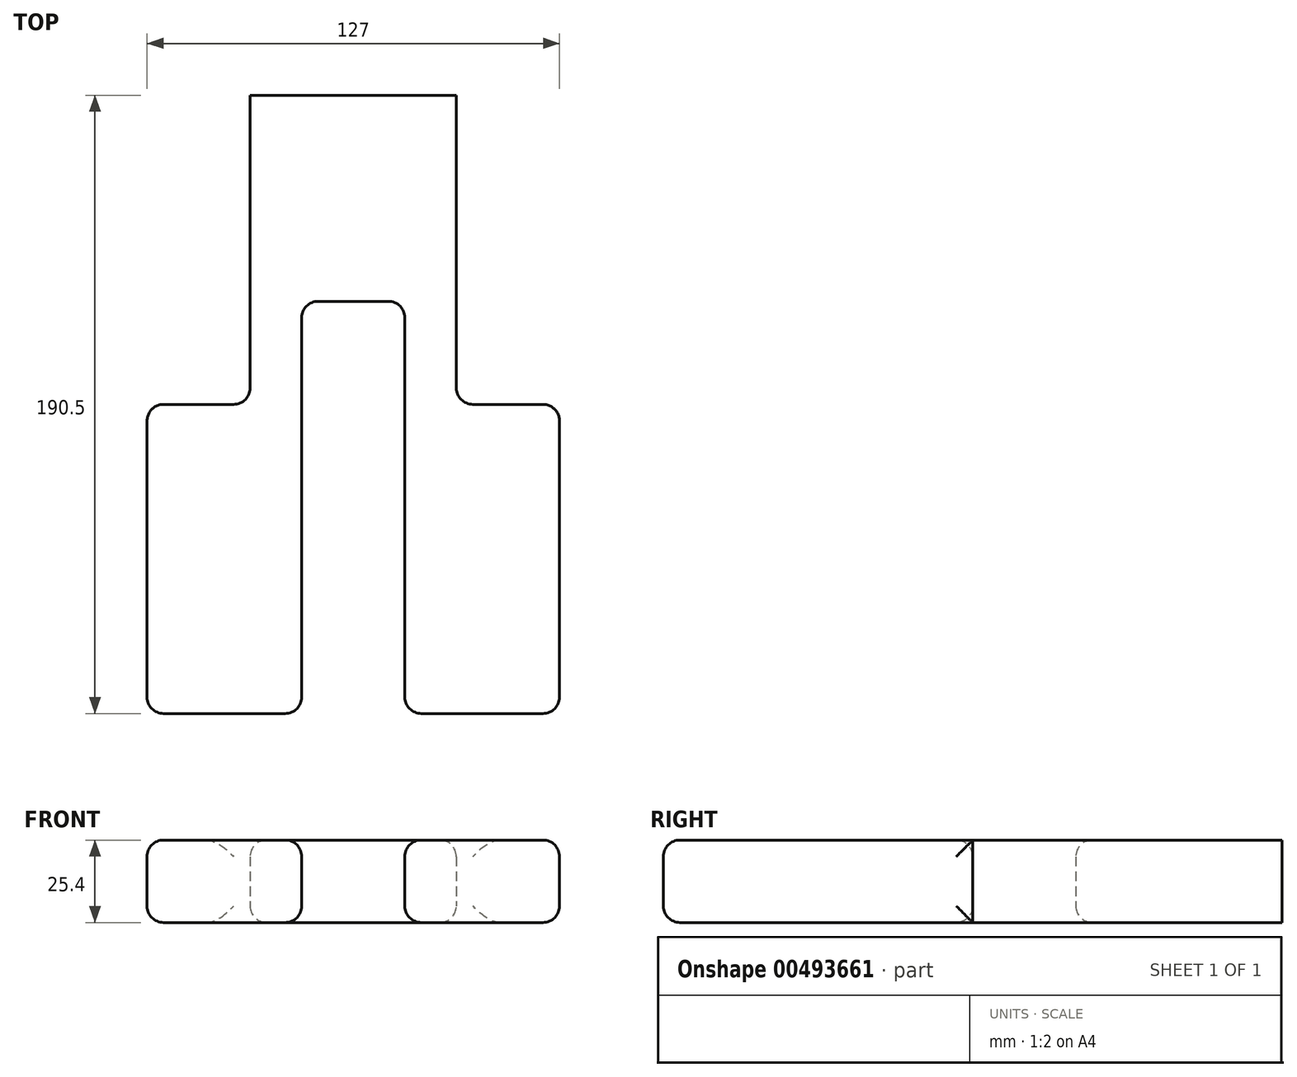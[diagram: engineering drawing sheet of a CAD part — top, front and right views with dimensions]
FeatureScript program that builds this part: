
annotation { "Feature Type Name" : "Feature", "Feature Type Description" : "" }
export const myFeature = defineFeature(function(context is Context, id is Id, definition is map)
    precondition{}
    {
        {
            var Q0;
            Q0=qCreatedBy(makeId("Top.planeOp"),FACE);
            var sketch = newSketch(context, id + "F0", { "sketchPlane" : qUnion([Q0])});
            skLineSegment(sketch, "E0", {"start": v(-48.62, 63.5) * mm, "end": v(-48.62, -31.75) * mm});
            skLineSegment(sketch, "E1", {"start": v(-48.62, -31.75) * mm, "end": v(-80.37, -31.75) * mm});
            skLineSegment(sketch, "E2", {"start": v(-80.37, -31.75) * mm, "end": v(-80.37, -127) * mm});
            skLineSegment(sketch, "E3", {"start": v(-80.37, -127) * mm, "end": v(-32.75, -127) * mm});
            skLineSegment(sketch, "E4", {"start": v(-32.75, -127) * mm, "end": v(-32.75, 0) * mm});
            skLineSegment(sketch, "E5", {"start": v(-32.75, 0) * mm, "end": v(-1, 0) * mm});
            skLineSegment(sketch, "E6", {"start": v(-1, 0) * mm, "end": v(-1, -127) * mm});
            skLineSegment(sketch, "E7", {"start": v(-1, -127) * mm, "end": v(46.63, -127) * mm});
            skLineSegment(sketch, "E8", {"start": v(46.63, -127) * mm, "end": v(46.63, -31.75) * mm});
            skLineSegment(sketch, "E9", {"start": v(46.63, -31.75) * mm, "end": v(14.88, -31.75) * mm});
            skLineSegment(sketch, "E10", {"start": v(14.88, -31.75) * mm, "end": v(14.88, 63.5) * mm});
            skLineSegment(sketch, "E11", {"start": v(14.88, 63.5) * mm, "end": v(-48.62, 63.5) * mm});
            skSolve(sketch);
        }
        {
            var Q0;
            Q0=makeQuery(id+"F0.imprint","IMPRINT",FACE,{"disambiguationData":[TD([[makeQuery(id+"F0.imprint","IMPRINT",EDGE,{"derivedFrom":sQuery(id+"F0.wireOp",EDGE,"E0")}),1.0]])]});
            extrude(context, id + "F1", {"entities" : qUnion([Q0]), "depth" : 25.4 * mm, "offsetDistance" : 25.4 * mm});
        }
        {
            var Q0;
            Q0=makeQuery(id+"F1.opExtrude","CAP_EDGE",EDGE,{"disambiguationData":[OSD([sQuery(id+"F0.wireOp",EDGE,"E10")])],"isStart":false});
            var Q1;
            Q1=makeQuery(id+"F1.opExtrude","CAP_EDGE",EDGE,{"disambiguationData":[OSD([sQuery(id+"F0.wireOp",EDGE,"E0")])],"isStart":false});
            var Q2;
            Q2=makeQuery(id+"F1.opExtrude","CAP_EDGE",EDGE,{"disambiguationData":[OSD([sQuery(id+"F0.wireOp",EDGE,"E0")])],"isStart":true});
            var Q3;
            Q3=makeQuery(id+"F1.opExtrude","CAP_EDGE",EDGE,{"disambiguationData":[OSD([sQuery(id+"F0.wireOp",EDGE,"E10")])],"isStart":true});
            var Q4;
            Q4=makeQuery(id+"F1.opExtrude","SWEPT_EDGE",EDGE,{"disambiguationData":[OSD([sQuery(id+"F0.wireOp",EDGE,"E9"),sQuery(id+"F0.wireOp",EDGE,"E10")])]});
            var Q5;
            Q5=makeQuery(id+"F1.opExtrude","SWEPT_EDGE",EDGE,{"disambiguationData":[OSD([sQuery(id+"F0.wireOp",EDGE,"E0"),sQuery(id+"F0.wireOp",EDGE,"E1")])]});
            var Q6;
            Q6=makeQuery(id+"F1.opExtrude","SWEPT_EDGE",EDGE,{"disambiguationData":[OSD([sQuery(id+"F0.wireOp",EDGE,"E1"),sQuery(id+"F0.wireOp",EDGE,"E2")])]});
            var Q7;
            Q7=makeQuery(id+"F1.opExtrude","CAP_EDGE",EDGE,{"disambiguationData":[OSD([sQuery(id+"F0.wireOp",EDGE,"E2")])],"isStart":false});
            var Q8;
            Q8=makeQuery(id+"F1.opExtrude","CAP_EDGE",EDGE,{"disambiguationData":[OSD([sQuery(id+"F0.wireOp",EDGE,"E2")])],"isStart":true});
            var Q9;
            Q9=makeQuery(id+"F1.opExtrude","CAP_EDGE",EDGE,{"disambiguationData":[OSD([sQuery(id+"F0.wireOp",EDGE,"E3")])],"isStart":false});
            var Q10;
            Q10=makeQuery(id+"F1.opExtrude","SWEPT_EDGE",EDGE,{"disambiguationData":[OSD([sQuery(id+"F0.wireOp",EDGE,"E2"),sQuery(id+"F0.wireOp",EDGE,"E3")])]});
            var Q11;
            Q11=makeQuery(id+"F1.opExtrude","CAP_EDGE",EDGE,{"disambiguationData":[OSD([sQuery(id+"F0.wireOp",EDGE,"E7")])],"isStart":false});
            var Q12;
            Q12=makeQuery(id+"F1.opExtrude","CAP_EDGE",EDGE,{"disambiguationData":[OSD([sQuery(id+"F0.wireOp",EDGE,"E8")])],"isStart":false});
            var Q13;
            Q13=makeQuery(id+"F1.opExtrude","SWEPT_FACE",FACE,{"disambiguationData":[OSD([sQuery(id+"F0.wireOp",EDGE,"E7")])]});
            var Q14;
            Q14=makeQuery(id+"F1.opExtrude","SWEPT_EDGE",EDGE,{"disambiguationData":[OSD([sQuery(id+"F0.wireOp",EDGE,"E3"),sQuery(id+"F0.wireOp",EDGE,"E4")])]});
            var Q15;
            Q15=makeQuery(id+"F1.opExtrude","CAP_EDGE",EDGE,{"disambiguationData":[OSD([sQuery(id+"F0.wireOp",EDGE,"E5")])],"isStart":false});
            var Q16;
            Q16=makeQuery(id+"F1.opExtrude","CAP_EDGE",EDGE,{"disambiguationData":[OSD([sQuery(id+"F0.wireOp",EDGE,"E4")])],"isStart":false});
            var Q17;
            Q17=makeQuery(id+"F1.opExtrude","CAP_EDGE",EDGE,{"disambiguationData":[OSD([sQuery(id+"F0.wireOp",EDGE,"E6")])],"isStart":false});
            var Q18;
            Q18=makeQuery(id+"F1.opExtrude","SWEPT_EDGE",EDGE,{"disambiguationData":[OSD([sQuery(id+"F0.wireOp",EDGE,"E8"),sQuery(id+"F0.wireOp",EDGE,"E9")])]});
            var Q19;
            Q19=makeQuery(id+"F1.opExtrude","CAP_EDGE",EDGE,{"disambiguationData":[OSD([sQuery(id+"F0.wireOp",EDGE,"E6")])],"isStart":true});
            var Q20;
            Q20=makeQuery(id+"F1.opExtrude","CAP_EDGE",EDGE,{"disambiguationData":[OSD([sQuery(id+"F0.wireOp",EDGE,"E5")])],"isStart":true});
            var Q21;
            Q21=makeQuery(id+"F1.opExtrude","CAP_EDGE",EDGE,{"disambiguationData":[OSD([sQuery(id+"F0.wireOp",EDGE,"E8")])],"isStart":true});
            var Q22;
            Q22=makeQuery(id+"F1.opExtrude","CAP_EDGE",EDGE,{"disambiguationData":[OSD([sQuery(id+"F0.wireOp",EDGE,"E4")])],"isStart":true});
            var Q23;
            Q23=makeQuery(id+"F1.opExtrude","SWEPT_FACE",FACE,{"disambiguationData":[OSD([sQuery(id+"F0.wireOp",EDGE,"E6")])]});
            var Q24;
            Q24=makeQuery(id+"F1.opExtrude","SWEPT_EDGE",EDGE,{"disambiguationData":[OSD([sQuery(id+"F0.wireOp",EDGE,"E4"),sQuery(id+"F0.wireOp",EDGE,"E5")])]});
            var Q25;
            Q25=makeQuery(id+"F1.opExtrude","CAP_EDGE",EDGE,{"disambiguationData":[OSD([sQuery(id+"F0.wireOp",EDGE,"E3")])],"isStart":true});
            fillet(context, id + "F2", {"entities" : qUnion([Q0, Q1, Q2, Q3, Q4, Q5, Q6, Q7, Q8, Q9, Q10, Q11, Q12, Q13, Q14, Q15, Q16, Q17, Q18, Q19, Q20, Q21, Q22, Q23, Q24, Q25]), "radius" : 5.08 * mm, "tangentPropagation" : true, "allowEdgeOverflow" : false});
        }
    });
